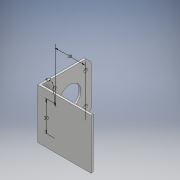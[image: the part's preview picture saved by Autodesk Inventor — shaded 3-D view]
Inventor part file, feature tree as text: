
AUTODESK INVENTOR PART (.ipt)
format: ipt  version: 2018 (Build 220112000, 112)  size: 141,312 bytes
history: native  units: mm
features: sketch x4, extrude x3
ambient origin geometry x8: Origin, YZ Plane, XZ Plane, XY Plane, X Axis, Y Axis, Z Axis, Center Point
bodies: Solid1 (feature_tree)
feature tree (7):
  extrude  "Extrusion1"  Depth=2.0mm
  extrude  "Extrusion2"  Depth=53.0mm
  extrude  "Extrusion3"  Depth=50.0mm
  sketch  "Sketch4"  dims[d9=3.5mm d10=31.0mm d11=31.0mm d12=21.0mm d13=50.0mm d14=0.0mm d15=45.0deg d16=5.0mm d17=50.0mm d18=0.0mm d19=4.2mm d20=30.0mm d21=30.0mm]
  sketch  "Sketch1"  dims[d1=51.0mm d2=2.0mm]
  sketch  "Sketch2"  dims[d4=2.0mm d5=53.0mm]
  sketch  "Sketch3"  dims[d6=50.0mm d7=0.0mm d8=22.1mm]
